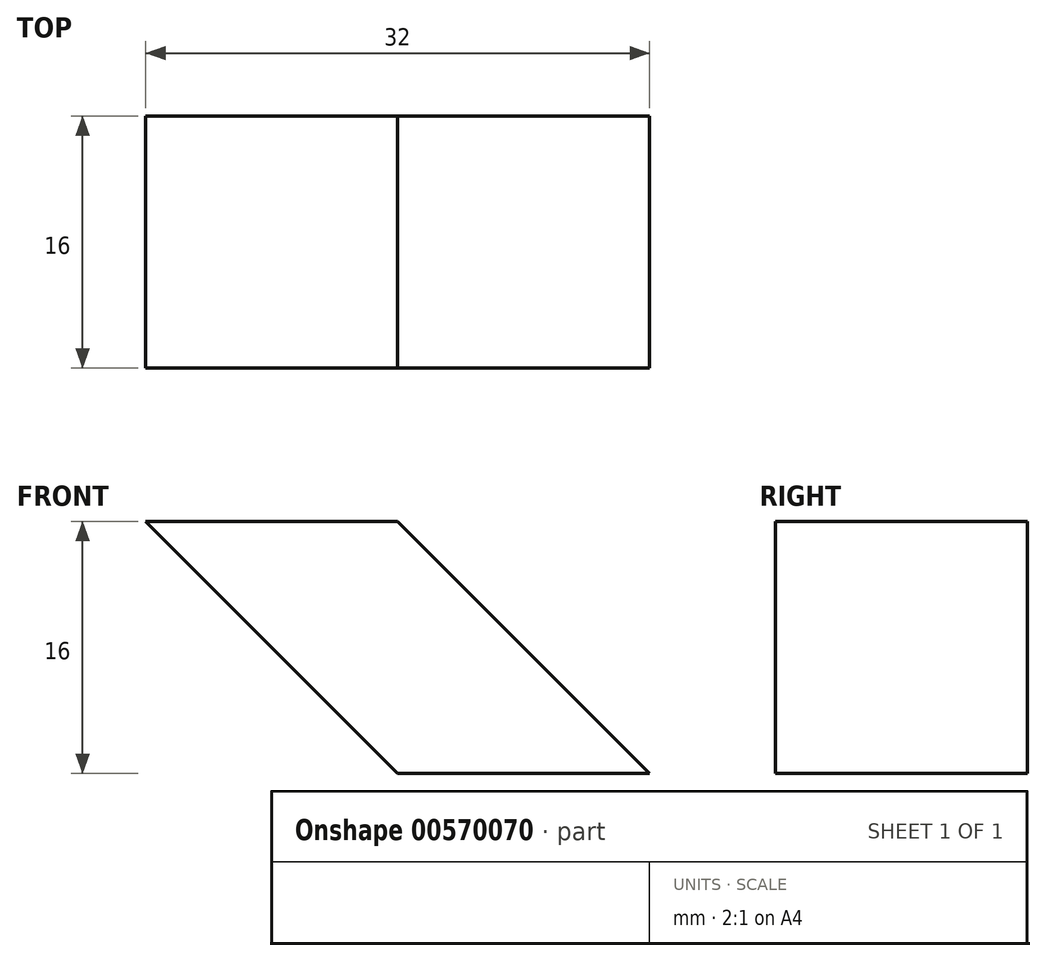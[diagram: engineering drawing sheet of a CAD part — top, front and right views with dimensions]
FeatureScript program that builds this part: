
annotation { "Feature Type Name" : "Feature", "Feature Type Description" : "" }
export const myFeature = defineFeature(function(context is Context, id is Id, definition is map)
    precondition{}
    {
        {
            var Q0;
            Q0=qCreatedBy(makeId("Top.planeOp"),FACE);
            var sketch = newSketch(context, id + "F0", { "sketchPlane" : qUnion([Q0])});
            skLineSegment(sketch, "E0.bottom", {"start": v(8, 8) * mm, "end": v(-8, 8) * mm});
            skLineSegment(sketch, "E0.top", {"start": v(8, -8) * mm, "end": v(-8, -8) * mm});
            skLineSegment(sketch, "E0.left", {"start": v(8, 8) * mm, "end": v(8, -8) * mm});
            skLineSegment(sketch, "E1.bottom", {"start": v(0, 8) * mm, "end": v(-16, 8) * mm});
            skLineSegment(sketch, "E1.top", {"start": v(0, -8) * mm, "end": v(-16, -8) * mm});
            skLineSegment(sketch, "E2.bottom", {"start": v(-8, 8) * mm, "end": v(-24, 8) * mm});
            skLineSegment(sketch, "E2.top", {"start": v(-8, -8) * mm, "end": v(-24, -8) * mm});
            skLineSegment(sketch, "E2.right", {"start": v(-24, 8) * mm, "end": v(-24, -8) * mm});
            skSolve(sketch);
        }
        {
            var Q0;
            Q0=makeQuery(id+"F0.imprint","IMPRINT",FACE,{"disambiguationData":[TD([[makeQuery(id+"F0.imprint","IMPRINT",EDGE,{"derivedFrom":sQuery(id+"F0.wireOp",EDGE,"E0.bottom")}),1.0]])]});
            extrude(context, id + "F1", {"entities" : qUnion([Q0]), "depth" : 16 * mm, "offsetDistance" : 25.4 * mm});
        }
        {
            var Q0;
            Q0=makeQuery(id+"F1.opExtrude","CAP_EDGE",EDGE,{"disambiguationData":[OSD([sQuery(id+"F0.wireOp",EDGE,"E0.left")])],"isStart":false});
            var Q1;
            Q1=makeQuery(id+"F1.opExtrude","CAP_EDGE",EDGE,{"disambiguationData":[OSD([sQuery(id+"F0.wireOp",EDGE,"E2.right")])],"isStart":true});
            chamfer(context, id + "F2", {"entities" : qUnion([Q0, Q1]), "width" : 16 * mm, "tangentPropagation" : true});
        }
    });
